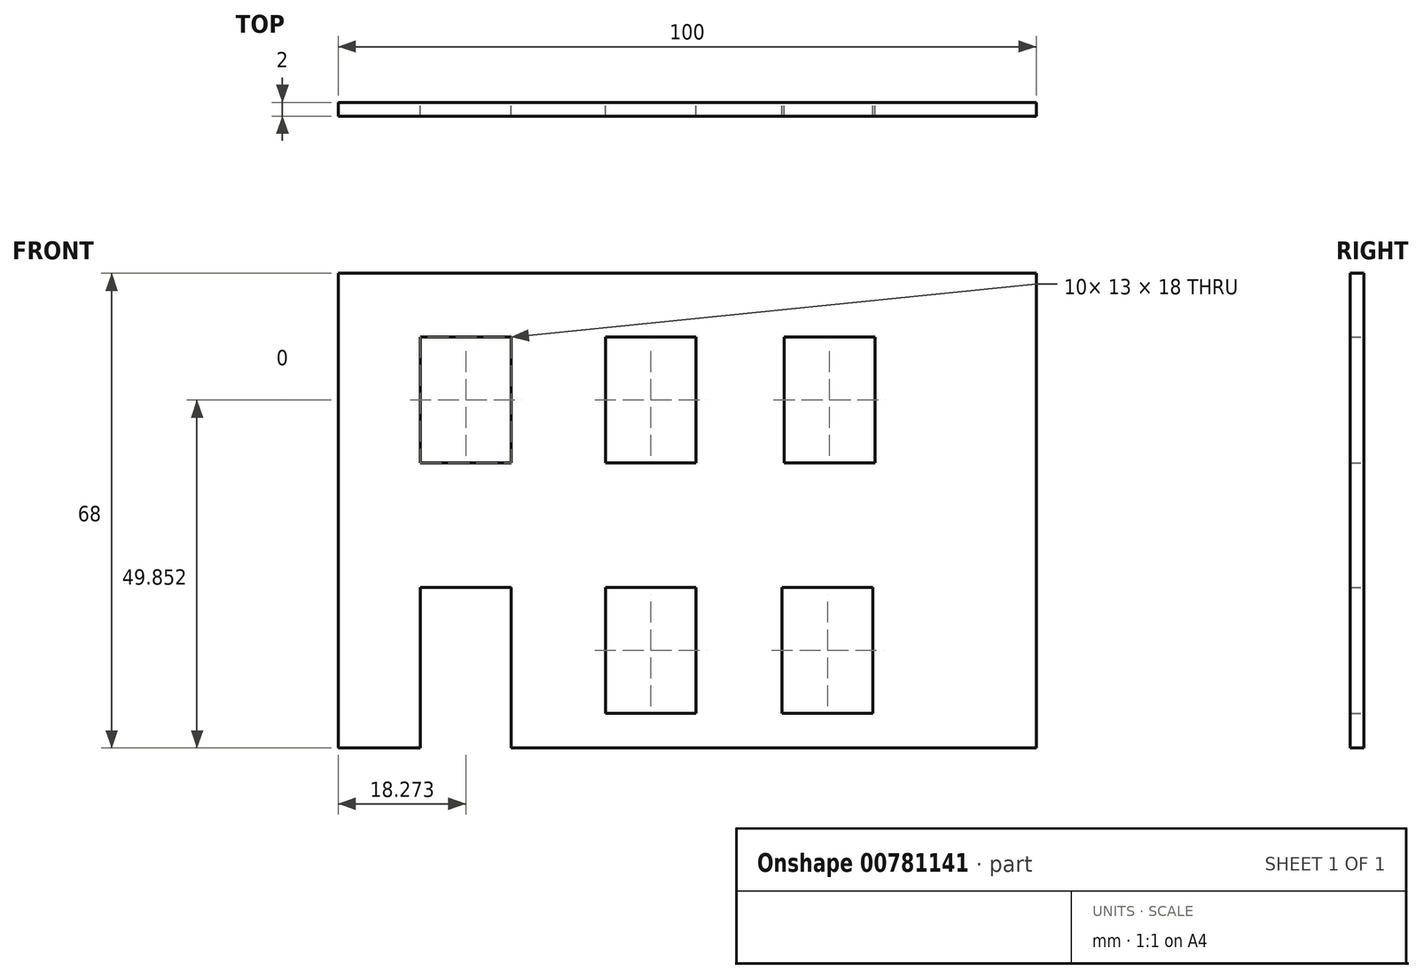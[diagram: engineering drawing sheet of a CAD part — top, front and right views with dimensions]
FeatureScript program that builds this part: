
annotation { "Feature Type Name" : "Feature", "Feature Type Description" : "" }
export const myFeature = defineFeature(function(context is Context, id is Id, definition is map)
    precondition{}
    {
        {
            var Q0;
            Q0=qCreatedBy(makeId("Front.planeOp"),FACE);
            var sketch = newSketch(context, id + "F0", { "sketchPlane" : qUnion([Q0])});
            skLineSegment(sketch, "E0.bottom", {"start": v(-38.27, 5.98) * mm, "end": v(61.73, 5.98) * mm});
            skLineSegment(sketch, "E0.top", {"start": v(-38.27, -62.02) * mm, "end": v(61.73, -62.02) * mm});
            skLineSegment(sketch, "E0.left", {"start": v(-38.27, 5.98) * mm, "end": v(-38.27, -62.02) * mm});
            skLineSegment(sketch, "E0.right", {"start": v(61.73, 5.98) * mm, "end": v(61.73, -62.02) * mm});
            skLineSegment(sketch, "E1.bottom", {"start": v(-26.5, -62.02) * mm, "end": v(-13.5, -62.02) * mm});
            skLineSegment(sketch, "E1.top", {"start": v(-26.5, -39.02) * mm, "end": v(-13.5, -39.02) * mm});
            skLineSegment(sketch, "E1.left", {"start": v(-26.5, -62.02) * mm, "end": v(-26.5, -39.02) * mm});
            skLineSegment(sketch, "E1.right", {"start": v(-13.5, -62.02) * mm, "end": v(-13.5, -39.02) * mm});
            skLineSegment(sketch, "E2.bottom", {"start": v(-26.5, -21.17) * mm, "end": v(-13.5, -21.17) * mm});
            skLineSegment(sketch, "E2.top", {"start": v(-26.5, -3.17) * mm, "end": v(-13.5, -3.17) * mm});
            skLineSegment(sketch, "E2.left", {"start": v(-26.5, -21.17) * mm, "end": v(-26.5, -3.17) * mm});
            skLineSegment(sketch, "E2.right", {"start": v(-13.5, -21.17) * mm, "end": v(-13.5, -3.17) * mm});
            skLineSegment(sketch, "E3.bottom", {"start": v(0, -39.02) * mm, "end": v(13, -39.02) * mm});
            skLineSegment(sketch, "E3.top", {"start": v(0, -57.02) * mm, "end": v(13, -57.02) * mm});
            skLineSegment(sketch, "E3.left", {"start": v(0, -39.02) * mm, "end": v(0, -57.02) * mm});
            skLineSegment(sketch, "E3.right", {"start": v(13, -39.02) * mm, "end": v(13, -57.02) * mm});
            skLineSegment(sketch, "E4.bottom", {"start": v(25.31, -39.02) * mm, "end": v(38.31, -39.02) * mm});
            skLineSegment(sketch, "E4.top", {"start": v(25.31, -57.02) * mm, "end": v(38.31, -57.02) * mm});
            skLineSegment(sketch, "E4.left", {"start": v(25.31, -39.02) * mm, "end": v(25.31, -57.02) * mm});
            skLineSegment(sketch, "E4.right", {"start": v(38.31, -39.02) * mm, "end": v(38.31, -57.02) * mm});
            skLineSegment(sketch, "E5.bottom", {"start": v(0, -3.17) * mm, "end": v(13, -3.17) * mm});
            skLineSegment(sketch, "E5.top", {"start": v(0, -21.17) * mm, "end": v(13, -21.17) * mm});
            skLineSegment(sketch, "E5.left", {"start": v(0, -3.17) * mm, "end": v(0, -21.17) * mm});
            skLineSegment(sketch, "E5.right", {"start": v(13, -3.17) * mm, "end": v(13, -21.17) * mm});
            skPoint(sketch, "E6.oppositeSnap0", {"position": v(6.5, -21.17) * mm});
            skLineSegment(sketch, "E6.bottom", {"start": v(25.6, -3.17) * mm, "end": v(38.6, -3.17) * mm});
            skLineSegment(sketch, "E6.top", {"start": v(25.6, -21.17) * mm, "end": v(38.6, -21.17) * mm});
            skLineSegment(sketch, "E6.left", {"start": v(25.6, -3.17) * mm, "end": v(25.6, -21.17) * mm});
            skLineSegment(sketch, "E6.right", {"start": v(38.6, -3.17) * mm, "end": v(38.6, -21.17) * mm});
            skSolve(sketch);
        }
        {
            var Q0;
            Q0=makeQuery(id+"F0.imprint","IMPRINT",FACE,{"disambiguationData":[TD([[makeQuery(id+"F0.imprint","IMPRINT",EDGE,{"derivedFrom":sQuery(id+"F0.wireOp",EDGE,"E0.bottom")}),-1.0]])]});
            extrude(context, id + "F1", {"entities" : qUnion([Q0]), "depth" : 2 * mm, "offsetDistance" : 25 * mm});
        }
    });
